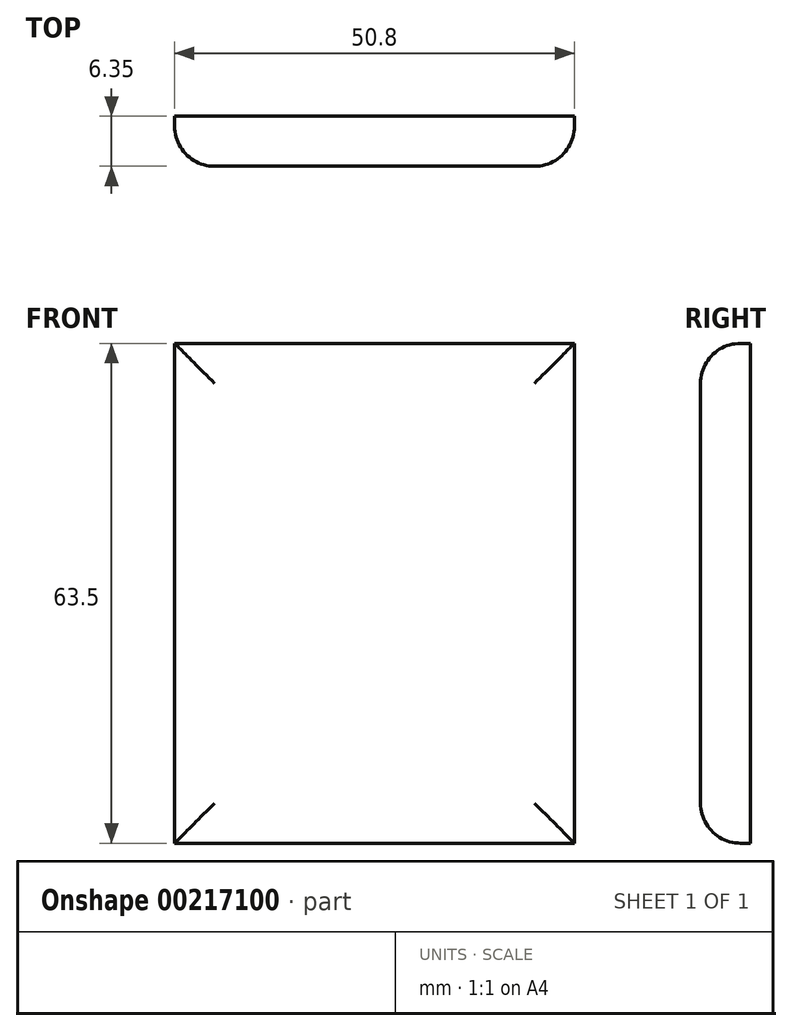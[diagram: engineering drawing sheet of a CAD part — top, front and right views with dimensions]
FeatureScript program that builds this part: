
annotation { "Feature Type Name" : "Feature", "Feature Type Description" : "" }
export const myFeature = defineFeature(function(context is Context, id is Id, definition is map)
    precondition{}
    {
        {
            var Q0;
            Q0=qCreatedBy(makeId("Front.planeOp"),FACE);
            var sketch = newSketch(context, id + "F0", { "sketchPlane" : qUnion([Q0])});
            skLineSegment(sketch, "E0.bottom", {"start": v(25.4, -31.75) * mm, "end": v(-25.4, -31.75) * mm});
            skLineSegment(sketch, "E0.top", {"start": v(25.4, 31.75) * mm, "end": v(-25.4, 31.75) * mm});
            skLineSegment(sketch, "E0.left", {"start": v(25.4, -31.75) * mm, "end": v(25.4, 31.75) * mm});
            skLineSegment(sketch, "E0.right", {"start": v(-25.4, -31.75) * mm, "end": v(-25.4, 31.75) * mm});
            skPoint(sketch, "E0.middle", {"position": v(0, 0) * mm});
            skSolve(sketch);
        }
        {
            var Q0;
            Q0=makeQuery(id+"F0.imprint","IMPRINT",FACE,{"disambiguationData":[TD([[makeQuery(id+"F0.imprint","IMPRINT",EDGE,{"derivedFrom":sQuery(id+"F0.wireOp",EDGE,"E0.bottom")}),-1.0]])]});
            extrude(context, id + "F1", {"entities" : qUnion([Q0]), "depth" : 6.35 * mm});
        }
        {
            var Q0;
            Q0=makeQuery(id+"F1.opExtrude","CAP_FACE",FACE,{"disambiguationData":[OSD([sQuery(id+"F0.wireOp",EDGE,"E0.bottom"),sQuery(id+"F0.wireOp",EDGE,"E0.top"),sQuery(id+"F0.wireOp",EDGE,"E0.left"),sQuery(id+"F0.wireOp",EDGE,"E0.right")])],"isStart":false});
            fillet(context, id + "F2", {"entities" : qUnion([Q0]), "radius" : 5.08 * mm, "tangentPropagation" : true, "allowEdgeOverflow" : false});
        }
    });
